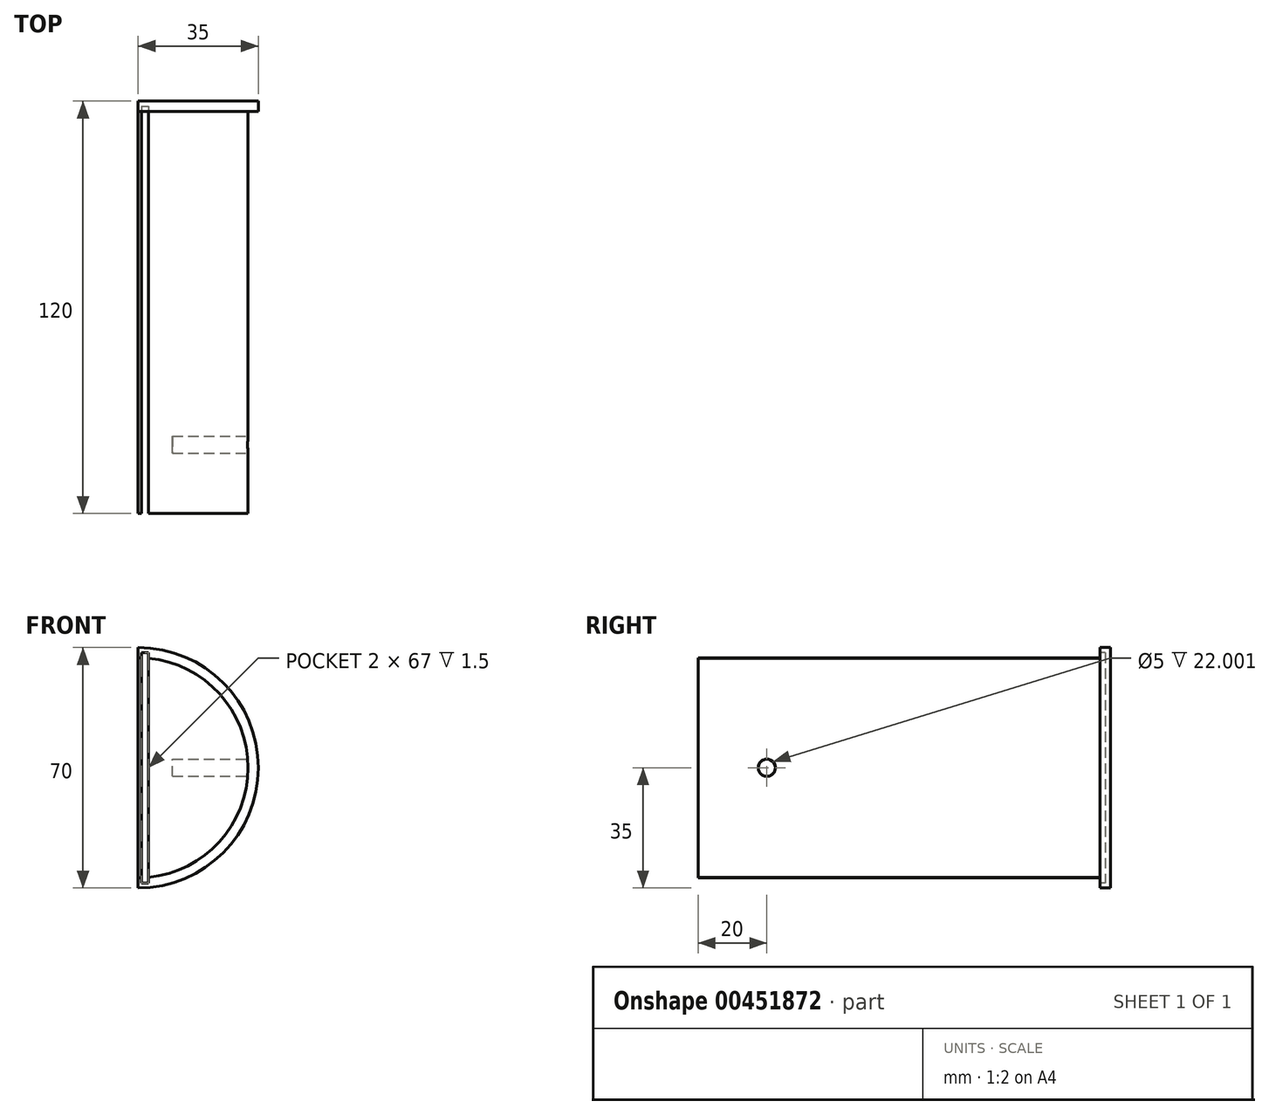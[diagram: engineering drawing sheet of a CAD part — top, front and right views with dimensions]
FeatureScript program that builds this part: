
annotation { "Feature Type Name" : "Feature", "Feature Type Description" : "" }
export const myFeature = defineFeature(function(context is Context, id is Id, definition is map)
    precondition{}
    {
        {
            var Q0;
            Q0=qCreatedBy(makeId("Front.planeOp"),FACE);
            var sketch = newSketch(context, id + "F0", { "sketchPlane" : qUnion([Q0])});
            skArc(sketch, "E0", {"start": v(0, 35) * mm, "mid": v(35, 0) * mm, "end": v(0, -35) * mm});
            skLineSegment(sketch, "E1", {"start": v(0, 35) * mm, "end": v(0, -35) * mm});
            skSolve(sketch);
        }
        {
            var Q0;
            Q0 = qSketchRegion(id + "F0", true);
            extrude(context, id + "F1", {"entities" : qUnion([Q0]), "depth" : 120 * mm});
        }
        {
            var Q0;
            Q0=makeQuery(id+"F1.opExtrude","CAP_FACE",FACE,{"disambiguationData":[OSD([sQuery(id+"F0.wireOp",EDGE,"E0"),sQuery(id+"F0.wireOp",EDGE,"E1")])],"isStart":false});
            var sketch = newSketch(context, id + "F2", { "sketchPlane" : qUnion([Q0])});
            skArc(sketch, "E2", {"start": v(0, 32) * mm, "mid": v(32, 0) * mm, "end": v(0, -32) * mm});
            skLineSegment(sketch, "E3", {"start": v(0, 32) * mm, "end": v(0, -32) * mm});
            skSolve(sketch);
        }
        {
            var Q0;
            Q0=makeQuery(id+"F2.imprint","IMPRINT",FACE,{"disambiguationData":[TD([[makeQuery(id+"F2.imprint","IMPRINT",EDGE,{"derivedFrom":sQuery(id+"F2.wireOp",EDGE,"E2")}),-1.0]])]});
            extrude(context, id + "F3", {"entities" : qUnion([Q0]), "operationType" : NewBodyOperationType.REMOVE, "oppositeDirection" : true, "depth" : 117 * mm});
        }
        {
            var Q0;
            Q0=makeQuery(id+"F1.opExtrude","CAP_FACE",FACE,{"disambiguationData":[OSD([sQuery(id+"F0.wireOp",EDGE,"E0"),sQuery(id+"F0.wireOp",EDGE,"E1")])],"isStart":false});
            var sketch = newSketch(context, id + "F4", { "sketchPlane" : qUnion([Q0])});
            skLineSegment(sketch, "E4.bottom", {"start": v(1, 33.5) * mm, "end": v(3, 33.5) * mm});
            skLineSegment(sketch, "E4.top", {"start": v(1, -33.5) * mm, "end": v(3, -33.5) * mm});
            skLineSegment(sketch, "E4.left", {"start": v(1, 33.5) * mm, "end": v(1, -33.5) * mm});
            skLineSegment(sketch, "E4.right", {"start": v(3, 33.5) * mm, "end": v(3, -33.5) * mm});
            skSolve(sketch);
        }
        {
            var Q0;
            {var subQ0=sQuery(id+"F4.wireOp",EDGE,"E4.left");var subQ1=makeQuery(id+"F3.boolean.opBoolean","COPY",EDGE,{"derivedFrom":makeQuery(id+"F3.opExtrude","CAP_EDGE",EDGE,{"disambiguationData":[OSD([sQuery(id+"F2.wireOp",EDGE,"E2")])],"isStart":true})});var subQ2=makeQuery(id+"F4.imprint","INTERSECT",VERTEX,{"disambiguationData":[OD(0.0)],"derivedFrom":[subQ1,subQ0]});Q0=makeQuery(id+"F4.imprint","IMPRINT",FACE,{"disambiguationData":[TD([[makeQuery(id+"F4.imprint","IMPRINT",EDGE,{"disambiguationData":[TD([[subQ2,-1.0]])],"derivedFrom":subQ0}),1.0]])]});}
            var Q1;
            {var subQ0=sQuery(id+"F4.wireOp",EDGE,"E4.bottom");Q1=makeQuery(id+"F4.imprint","IMPRINT",FACE,{"disambiguationData":[TD([[makeQuery(id+"F4.imprint","IMPRINT",EDGE,{"derivedFrom":subQ0}),-1.0]])]});}
            var Q2;
            {var subQ0=sQuery(id+"F4.wireOp",EDGE,"E4.top");Q2=makeQuery(id+"F4.imprint","IMPRINT",FACE,{"disambiguationData":[TD([[makeQuery(id+"F4.imprint","IMPRINT",EDGE,{"derivedFrom":subQ0}),1.0]])]});}
            extrude(context, id + "F5", {"entities" : qUnion([Q0, Q1, Q2]), "operationType" : NewBodyOperationType.REMOVE, "oppositeDirection" : true, "depth" : 118.5 * mm});
        }
        {
            var Q0;
            Q0=qCreatedBy(makeId("Top.planeOp"),FACE);
            var sketch = newSketch(context, id + "F6", { "sketchPlane" : qUnion([Q0])});
            skLineSegment(sketch, "E5", {"start": v(35, 0) * mm, "end": v(35, -168.9) * mm});
            skSolve(sketch);
        }
        {
            var Q0;
            Q0=sQuery(id+"F6.wireOp",EDGE,"E5");
            cPlane(context, id + "F7", {"entities" : qUnion([Q0]), "cplaneType" : CPlaneType.LINE_ANGLE, "offset" : 25 * mm, "angle" : 90 * degree, "width" : 150 * mm, "height" : 150 * mm});
        }
        {
            var Q0;
            Q0=qCreatedBy(id+"F7.planeOp",FACE);
            var sketch = newSketch(context, id + "F8", { "sketchPlane" : qUnion([Q0])});
            skCircle(sketch, "E6", {"center": v(-100, 0) * mm, "radius": 2.5 * mm});
            skSolve(sketch);
        }
        {
            var Q0;
            Q0 = qSketchRegion(id + "F8", true);
            extrude(context, id + "F9", {"entities" : qUnion([Q0]), "operationType" : NewBodyOperationType.REMOVE, "oppositeDirection" : true, "depth" : 25 * mm});
        }
    });
